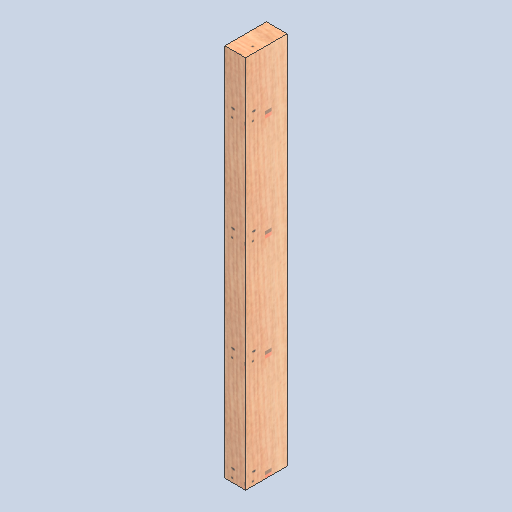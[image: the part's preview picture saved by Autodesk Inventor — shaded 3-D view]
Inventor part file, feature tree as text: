
AUTODESK INVENTOR PART (.ipt)
format: ipt  version: 2025 (Build 290162000, 162)  size: 151,040 bytes
history: native  units: in
note: dims shown in document units (in); Inventor stores cm internally (conversion verified against a paired STEP export)
features: extrude x1, sketch x1
ambient origin geometry x8: Origin, YZ Plane, XZ Plane, XY Plane, X Axis, Y Axis, Z Axis, Center Point
bodies: Solid1 (feature_tree)
feature tree (2):
  extrude  "Extrusion1"  Depth=4.0in
  sketch  "Sketch1"  dims[d0=2.0in d1=4.0in d2=36.0in d3=0.0in]
